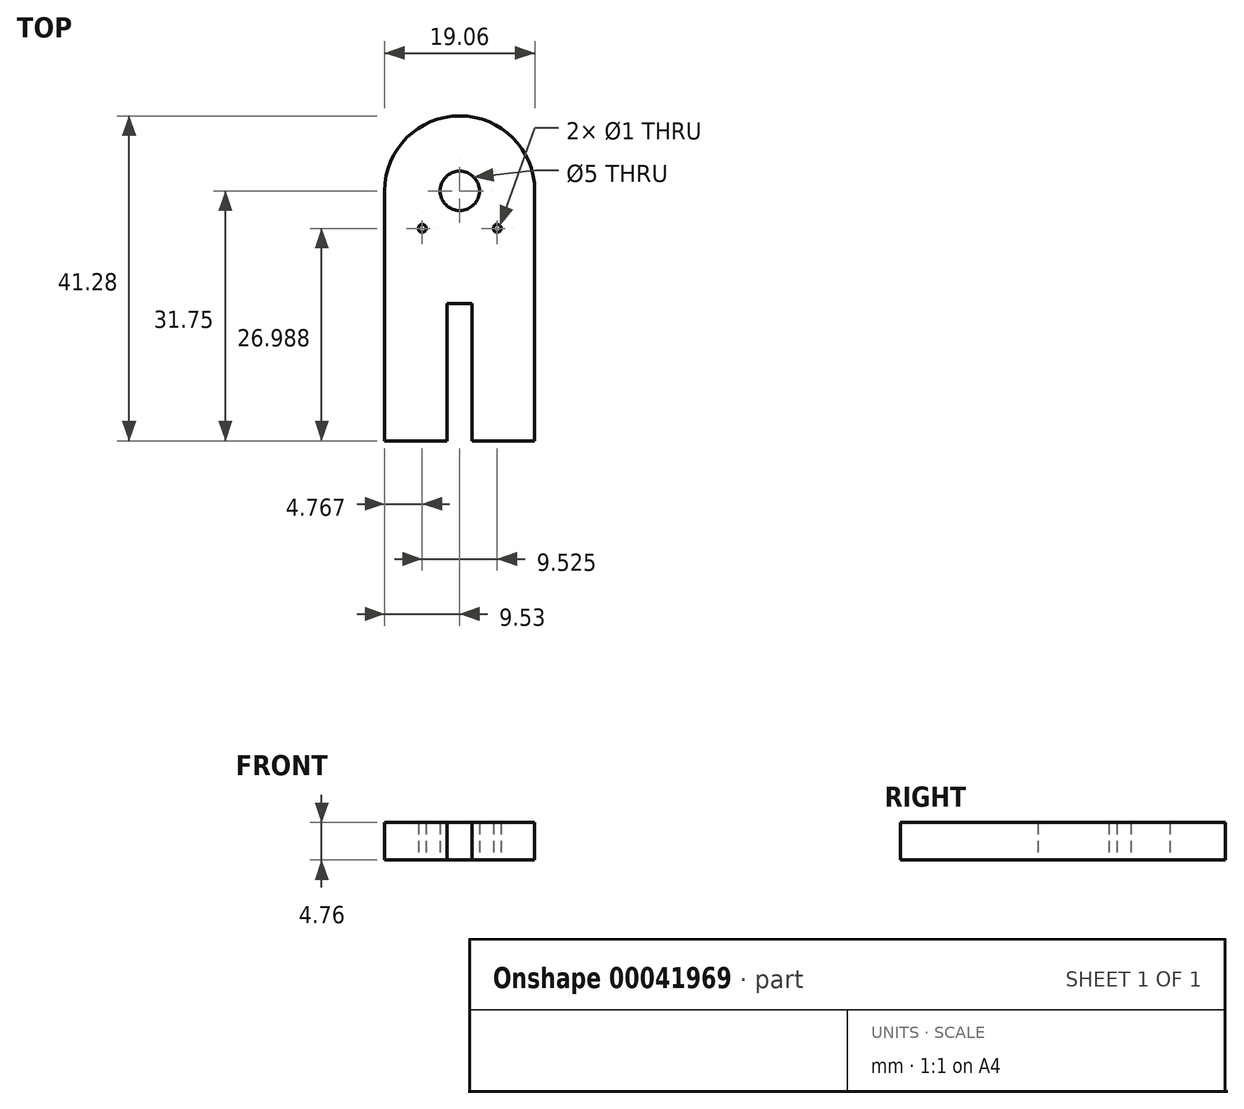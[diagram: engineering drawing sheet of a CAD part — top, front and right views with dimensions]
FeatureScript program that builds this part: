
annotation { "Feature Type Name" : "Feature", "Feature Type Description" : "" }
export const myFeature = defineFeature(function(context is Context, id is Id, definition is map)
    precondition{}
    {
        {
            var Q0;
            Q0=qCreatedBy(makeId("Top.planeOp"),FACE);
            var sketch = newSketch(context, id + "F0", { "sketchPlane" : qUnion([Q0])});
            skArc(sketch, "E0", {"start": v(9.53, 0) * mm, "mid": v(0, 9.53) * mm, "end": v(-9.53, 0) * mm});
            skLineSegment(sketch, "E1", {"start": v(-9.53, 0) * mm, "end": v(-9.53, -31.75) * mm});
            skLineSegment(sketch, "E2", {"start": v(9.53, 0) * mm, "end": v(9.53, -31.75) * mm});
            skLineSegment(sketch, "E3", {"start": v(-9.53, -31.75) * mm, "end": v(-1.59, -31.75) * mm});
            skCircle(sketch, "E4", {"center": v(0, 0) * mm, "radius": 2.5 * mm});
            skLineSegment(sketch, "E5", {"start": v(-1.59, -31.75) * mm, "end": v(-1.59, -14.29) * mm});
            skLineSegment(sketch, "E6", {"start": v(1.59, -31.75) * mm, "end": v(1.59, -14.29) * mm});
            skLineSegment(sketch, "E7", {"start": v(1.59, -14.29) * mm, "end": v(-1.59, -14.29) * mm});
            skPoint(sketch, "E8.center.orphan", {"position": v(0, -31.75) * mm});
            skLineSegment(sketch, "E9.trimOffspring", {"start": v(1.59, -31.75) * mm, "end": v(9.53, -31.75) * mm});
            skCircle(sketch, "E10", {"center": v(-4.76, -4.76) * mm, "radius": 0.5 * mm});
            skCircle(sketch, "E11.MirrorC", {"center": v(4.76, -4.76) * mm, "radius": 0.5 * mm});
            skSolve(sketch);
        }
        {
            var Q0;
            Q0=makeQuery(id+"F0.imprint","IMPRINT",FACE,{"disambiguationData":[TD([[makeQuery(id+"F0.imprint","IMPRINT",EDGE,{"derivedFrom":sQuery(id+"F0.wireOp",EDGE,"E0")}),1.0]])]});
            extrude(context, id + "F1", {"entities" : qUnion([Q0]), "depth" : 4.76 * mm});
        }
    });
